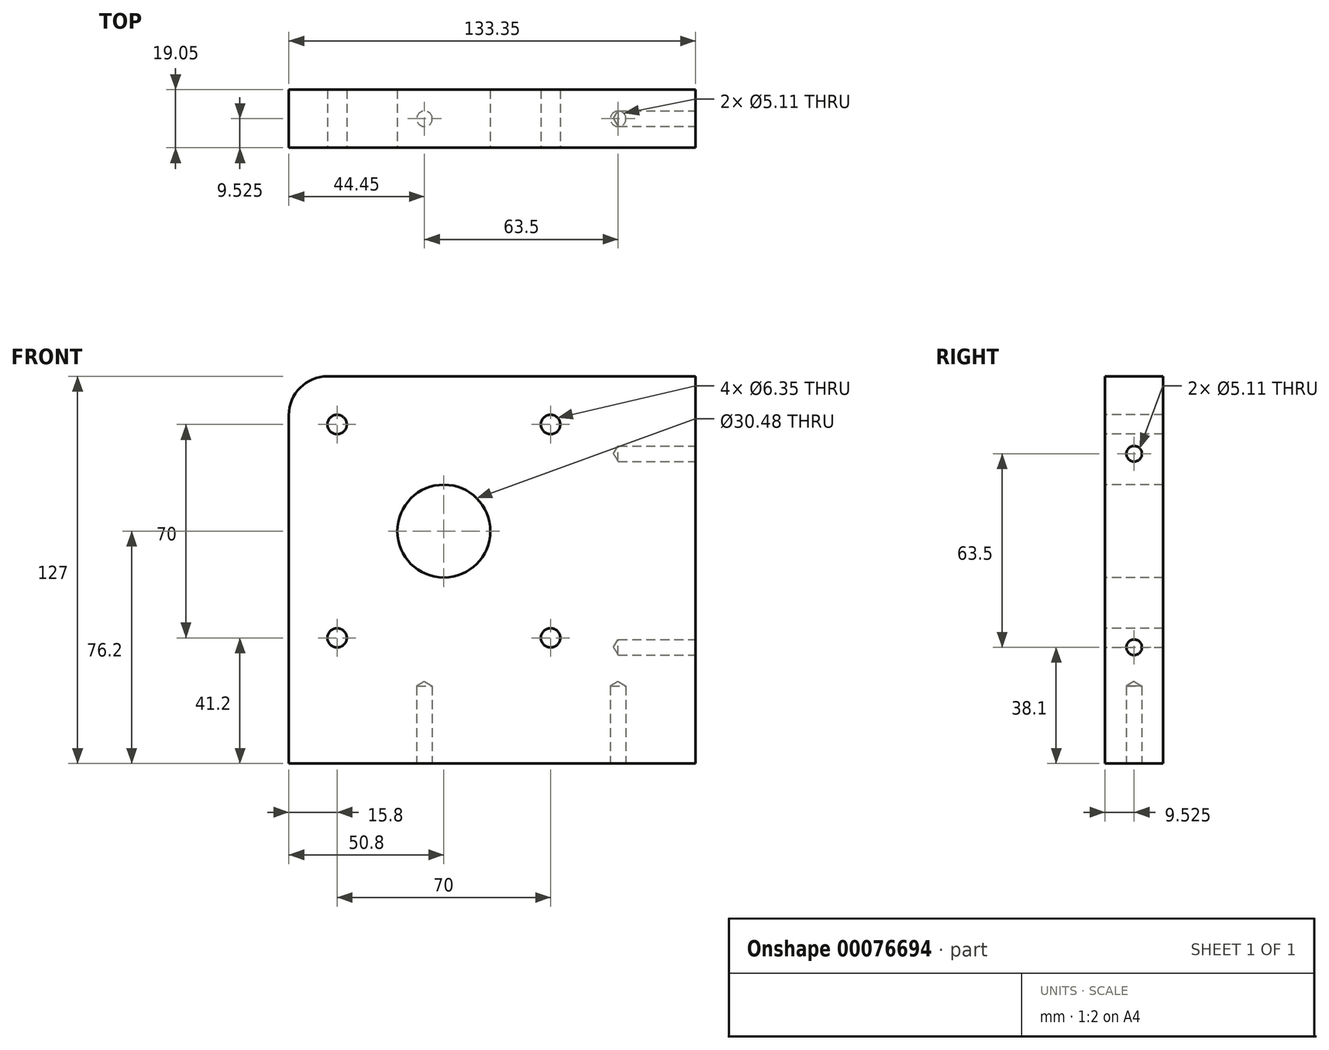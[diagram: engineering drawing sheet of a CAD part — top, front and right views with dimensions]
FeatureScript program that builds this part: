
annotation { "Feature Type Name" : "Feature", "Feature Type Description" : "" }
export const myFeature = defineFeature(function(context is Context, id is Id, definition is map)
    precondition{}
    {
        {
            var Q0;
            Q0=qCreatedBy(makeId("Front.planeOp"),FACE);
            var sketch = newSketch(context, id + "F0", { "sketchPlane" : qUnion([Q0])});
            skLineSegment(sketch, "E0.bottom", {"start": v(0, 0) * mm, "end": v(-133.35, 0) * mm});
            skLineSegment(sketch, "E0.top", {"start": v(0, 127) * mm, "end": v(-133.35, 127) * mm});
            skLineSegment(sketch, "E0.left", {"start": v(0, 0) * mm, "end": v(0, 127) * mm});
            skLineSegment(sketch, "E1.0", {"start": v(-82.55, 0) * mm, "end": v(-82.55, 127) * mm, "construction": true});
            skLineSegment(sketch, "E2.0", {"start": v(0, 76.2) * mm, "end": v(-127, 76.2) * mm, "construction": true});
            skCircle(sketch, "E3", {"center": v(-82.55, 76.2) * mm, "radius": 15.24 * mm});
            skLineSegment(sketch, "E4.0", {"start": v(-117.55, 0) * mm, "end": v(-117.55, 127) * mm, "construction": true});
            skLineSegment(sketch, "E5.0", {"start": v(0, 111.2) * mm, "end": v(-127, 111.2) * mm, "construction": true});
            skLineSegment(sketch, "E6.0", {"start": v(0, 41.2) * mm, "end": v(-127, 41.2) * mm, "construction": true});
            skCircle(sketch, "E7", {"center": v(-117.55, 111.2) * mm, "radius": 3.18 * mm});
            skCircle(sketch, "E8", {"center": v(-47.55, 111.2) * mm, "radius": 3.18 * mm});
            skCircle(sketch, "E9", {"center": v(-47.55, 41.2) * mm, "radius": 3.18 * mm});
            skCircle(sketch, "E10", {"center": v(-117.55, 41.2) * mm, "radius": 3.18 * mm});
            skLineSegment(sketch, "E11.0", {"start": v(-133.35, 0) * mm, "end": v(-133.35, 127) * mm});
            skSolve(sketch);
        }
        {
            var Q0;
            Q0=makeQuery(id+"F0.imprint","IMPRINT",FACE,{"disambiguationData":[TD([[makeQuery(id+"F0.imprint","IMPRINT",EDGE,{"derivedFrom":sQuery(id+"F0.wireOp",EDGE,"E0.bottom")}),-1.0]])]});
            extrude(context, id + "F1", {"entities" : qUnion([Q0]), "depth" : 19.05 * mm});
        }
        {
            var Q0;
            Q0=makeQuery(id+"F1.opExtrude","SWEPT_FACE",FACE,{"disambiguationData":[OSD([sQuery(id+"F0.wireOp",EDGE,"E0.left")])]});
            var sketch = newSketch(context, id + "F2", { "sketchPlane" : qUnion([Q0])});
            skLineSegment(sketch, "E12.0", {"start": v(-19.05, 38.1) * mm, "end": v(0, 38.1) * mm, "construction": true});
            skLineSegment(sketch, "E13.0", {"start": v(-19.05, 101.6) * mm, "end": v(0, 101.6) * mm, "construction": true});
            skCircle(sketch, "E14", {"center": v(-9.53, 101.6) * mm, "radius": 2.55 * mm, "construction": true});
            skCircle(sketch, "E15", {"center": v(-9.53, 38.1) * mm, "radius": 2.55 * mm, "construction": true});
            skSolve(sketch);
        }
        {
            var Q0;
            Q0=makeQuery(id+"F1.opExtrude","SWEPT_FACE",FACE,{"disambiguationData":[OSD([sQuery(id+"F0.wireOp",EDGE,"E0.bottom")])]});
            var sketch = newSketch(context, id + "F3", { "sketchPlane" : qUnion([Q0])});
            skLineSegment(sketch, "E16.0", {"start": v(-25.4, 19.05) * mm, "end": v(-25.4, 0) * mm, "construction": true});
            skLineSegment(sketch, "E17.0", {"start": v(-88.9, 19.05) * mm, "end": v(-88.9, 0) * mm, "construction": true});
            skCircle(sketch, "E18", {"center": v(-25.4, 9.53) * mm, "radius": 2.55 * mm, "construction": true});
            skCircle(sketch, "E19", {"center": v(-88.9, 9.53) * mm, "radius": 2.55 * mm, "construction": true});
            skSolve(sketch);
        }
        {
            var Q0;
            Q0=sQuery(id+"F2.wireOp",VERTEX,"E14.center");
            var Q1;
            Q1=sQuery(id+"F2.wireOp",VERTEX,"E15.center");
            var Q2;
            Q2=sQuery(id+"F3.wireOp",VERTEX,"E18.center");
            var Q3;
            Q3=sQuery(id+"F3.wireOp",VERTEX,"E19.center");
            var Q4;
            Q4=makeQuery(id+"F1.opExtrude","SWEPT_BODY",BODY,{"disambiguationData":[OSD([sQuery(id+"F0.wireOp",EDGE,"E0.bottom"),sQuery(id+"F0.wireOp",EDGE,"E0.top"),sQuery(id+"F0.wireOp",EDGE,"E0.left"),sQuery(id+"F0.wireOp",EDGE,"E0.right"),sQuery(id+"F0.wireOp",EDGE,"E3"),sQuery(id+"F0.wireOp",EDGE,"nUcfbkLc-Mws5-BHbQ-38nk-U2GFuzRH0i70"),sQuery(id+"F0.wireOp",EDGE,"KiZFqfh8-50TI-2G5C-Q8pB-eBEgE6UAUp9d"),sQuery(id+"F0.wireOp",EDGE,"jryU284U-9RFU-iTRo-rFwV-bFfDN96uC7nc"),sQuery(id+"F0.wireOp",EDGE,"zIxsMsRn-I19k-2vYv-R56y-sKz7VPmyEsYo")])]});
            hole(context, id + "F4", {"style" : HoleStyle.SIMPLE, "endStyle" : HoleEndStyle.BLIND, "holeDiameter" : 5.1 * mm, "holeDepth" : 25.4 * mm, "locations" : qUnion([Q0, Q1, Q2, Q3]), "scope" : qUnion([Q4])});
        }
        {
            var Q0;
            Q0=makeQuery(id+"F1.opExtrude","SWEPT_BODY",BODY,{"disambiguationData":[OSD([sQuery(id+"F0.wireOp",EDGE,"E0.bottom"),sQuery(id+"F0.wireOp",EDGE,"E0.top"),sQuery(id+"F0.wireOp",EDGE,"E0.left"),sQuery(id+"F0.wireOp",EDGE,"E0.right"),sQuery(id+"F0.wireOp",EDGE,"E3"),sQuery(id+"F0.wireOp",EDGE,"nUcfbkLc-Mws5-BHbQ-38nk-U2GFuzRH0i70"),sQuery(id+"F0.wireOp",EDGE,"KiZFqfh8-50TI-2G5C-Q8pB-eBEgE6UAUp9d"),sQuery(id+"F0.wireOp",EDGE,"jryU284U-9RFU-iTRo-rFwV-bFfDN96uC7nc"),sQuery(id+"F0.wireOp",EDGE,"zIxsMsRn-I19k-2vYv-R56y-sKz7VPmyEsYo")])]});
            var Q1;
            Q1=makeQuery(id+"F1.opExtrude","CAP_FACE",FACE,{"disambiguationData":[OSD([sQuery(id+"F0.wireOp",EDGE,"E0.bottom"),sQuery(id+"F0.wireOp",EDGE,"E0.top"),sQuery(id+"F0.wireOp",EDGE,"E0.left"),sQuery(id+"F0.wireOp",EDGE,"E0.right"),sQuery(id+"F0.wireOp",EDGE,"E3"),sQuery(id+"F0.wireOp",EDGE,"nUcfbkLc-Mws5-BHbQ-38nk-U2GFuzRH0i70"),sQuery(id+"F0.wireOp",EDGE,"KiZFqfh8-50TI-2G5C-Q8pB-eBEgE6UAUp9d"),sQuery(id+"F0.wireOp",EDGE,"jryU284U-9RFU-iTRo-rFwV-bFfDN96uC7nc"),sQuery(id+"F0.wireOp",EDGE,"zIxsMsRn-I19k-2vYv-R56y-sKz7VPmyEsYo")])],"isStart":false});
            mirror(context, id + "F5", {"entities" : qUnion([Q0]), "mirrorPlane" : qUnion([Q1])});
        }
        {
            var Q0;
            Q0=makeQuery(id+"F1.opExtrude","SWEPT_BODY",BODY,{"disambiguationData":[OSD([sQuery(id+"F0.wireOp",EDGE,"E0.bottom"),sQuery(id+"F0.wireOp",EDGE,"E0.top"),sQuery(id+"F0.wireOp",EDGE,"E0.left"),sQuery(id+"F0.wireOp",EDGE,"E0.right"),sQuery(id+"F0.wireOp",EDGE,"E3"),sQuery(id+"F0.wireOp",EDGE,"nUcfbkLc-Mws5-BHbQ-38nk-U2GFuzRH0i70"),sQuery(id+"F0.wireOp",EDGE,"KiZFqfh8-50TI-2G5C-Q8pB-eBEgE6UAUp9d"),sQuery(id+"F0.wireOp",EDGE,"jryU284U-9RFU-iTRo-rFwV-bFfDN96uC7nc"),sQuery(id+"F0.wireOp",EDGE,"zIxsMsRn-I19k-2vYv-R56y-sKz7VPmyEsYo")])]});
            deleteBodies(context, id + "F6", {"entities" : qUnion([Q0])});
        }
        {
            var Q0;
            Q0=makeQuery(id+"F5.opPattern","COPY",EDGE,{"derivedFrom":makeQuery(id+"F1.opExtrude","SWEPT_EDGE",EDGE,{"disambiguationData":[OSD([sQuery(id+"F0.wireOp",EDGE,"E0.top"),sQuery(id+"F0.wireOp",EDGE,"E11.0")])]}),"instanceName":"1"});
            fillet(context, id + "F7", {"entities" : qUnion([Q0]), "radius" : 12.7 * mm, "tangentPropagation" : true, "allowEdgeOverflow" : false});
        }
    });
